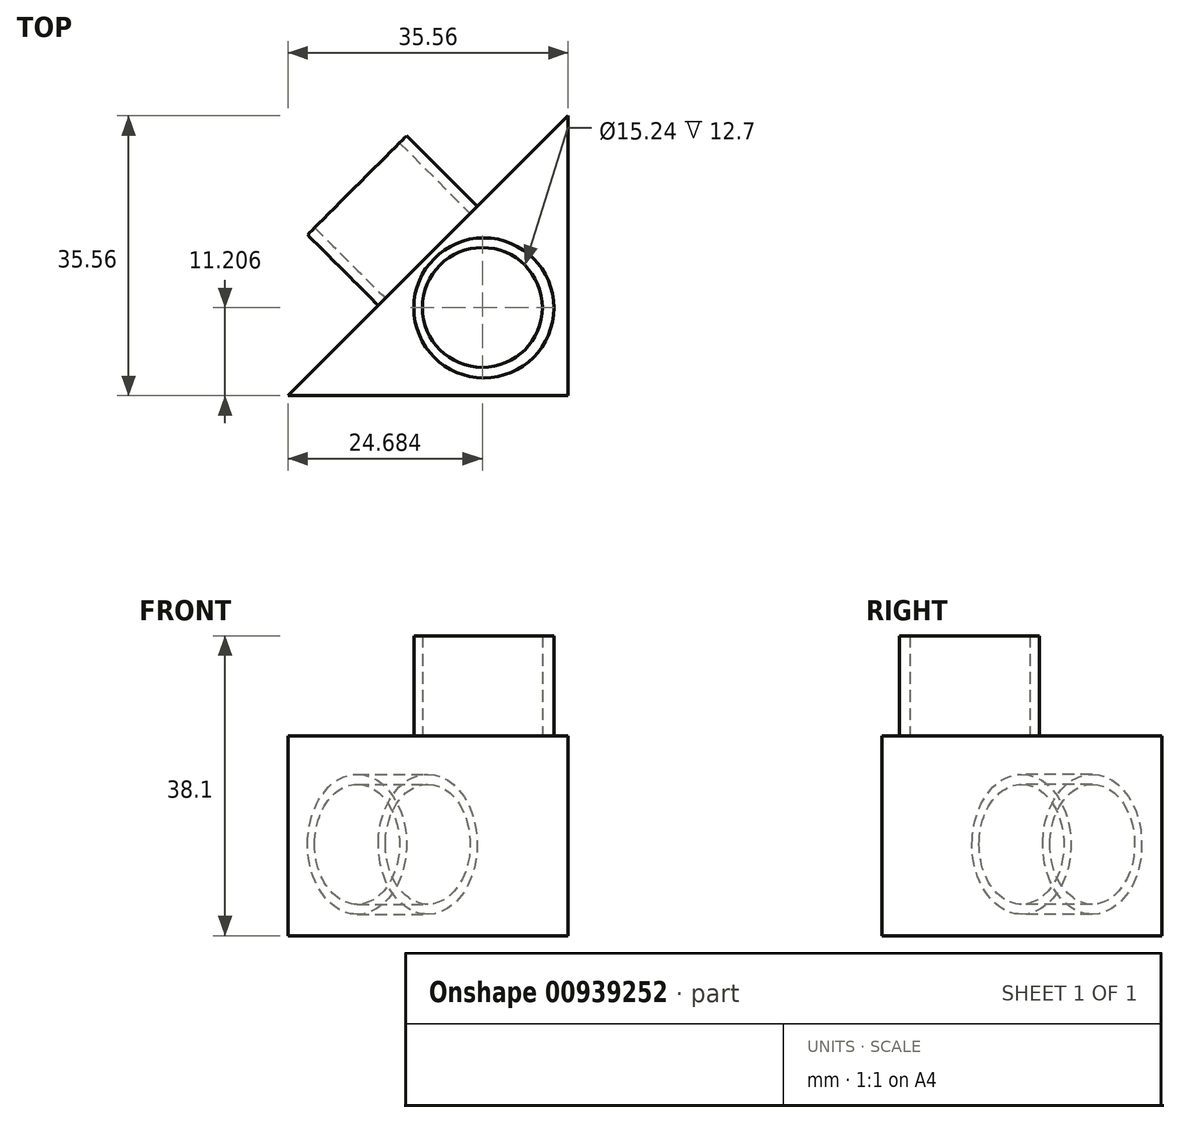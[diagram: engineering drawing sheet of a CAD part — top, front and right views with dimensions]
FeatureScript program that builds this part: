
annotation { "Feature Type Name" : "Feature", "Feature Type Description" : "" }
export const myFeature = defineFeature(function(context is Context, id is Id, definition is map)
    precondition{}
    {
        {
            var Q0;
            Q0=qCreatedBy(makeId("Top.planeOp"),FACE);
            var sketch = newSketch(context, id + "F0", { "sketchPlane" : qUnion([Q0])});
            skLineSegment(sketch, "E0", {"start": v(-60.17, 0) * mm, "end": v(-24.61, 35.56) * mm});
            skLineSegment(sketch, "E1", {"start": v(-24.61, 35.56) * mm, "end": v(-24.61, 0) * mm});
            skLineSegment(sketch, "E2", {"start": v(-24.61, 0) * mm, "end": v(-60.17, 0) * mm});
            skSolve(sketch);
        }
        {
            var Q0;
            Q0=makeQuery(id+"F0.imprint","IMPRINT",FACE,{"disambiguationData":[TD([[makeQuery(id+"F0.imprint","IMPRINT",EDGE,{"derivedFrom":sQuery(id+"F0.wireOp",EDGE,"E0")}),-1.0]])]});
            extrude(context, id + "F1", {"entities" : qUnion([Q0]), "depth" : 25.4 * mm, "offsetDistance" : 25.4 * mm});
        }
        {
            var Q0;
            Q0=makeQuery(id+"F1.opExtrude","CAP_FACE",FACE,{"disambiguationData":[OSD([sQuery(id+"F0.wireOp",EDGE,"E0"),sQuery(id+"F0.wireOp",EDGE,"E1"),sQuery(id+"F0.wireOp",EDGE,"E2")])],"isStart":false});
            var sketch = newSketch(context, id + "F2", { "sketchPlane" : qUnion([Q0])});
            skCircle(sketch, "E3", {"center": v(-35.49, 11.2) * mm, "radius": 7.62 * mm});
            skSolve(sketch);
        }
        {
            var Q0;
            Q0=makeQuery(id+"F2.imprint","IMPRINT",FACE,{"disambiguationData":[TD([[makeQuery(id+"F2.imprint","IMPRINT",EDGE,{"derivedFrom":sQuery(id+"F2.wireOp",EDGE,"E3")}),-1.0]])]});
            var sketch = newSketch(context, id + "F3", { "sketchPlane" : qUnion([Q0])});
            skCircle(sketch, "E4", {"center": v(-35.3, 11.16) * mm, "radius": 8.9 * mm});
            skSolve(sketch);
        }
        {
            var Q0;
            Q0 = qSketchRegion(id + "F3", true);
            extrude(context, id + "F4", {"entities" : qUnion([Q0]), "operationType" : NewBodyOperationType.ADD, "depth" : 12.7 * mm, "offsetDistance" : 25.4 * mm});
        }
        {
            var Q0;
            Q0 = qSketchRegion(id + "F2", true);
            extrude(context, id + "F5", {"entities" : qUnion([Q0]), "operationType" : NewBodyOperationType.REMOVE, "depth" : 39.12 * mm, "offsetDistance" : 25.4 * mm});
        }
        {
            var Q0;
            Q0=makeQuery(id+"F1.opExtrude","SWEPT_FACE",FACE,{"disambiguationData":[OSD([sQuery(id+"F0.wireOp",EDGE,"E0")])]});
            var sketch = newSketch(context, id + "F6", { "sketchPlane" : qUnion([Q0])});
            skCircle(sketch, "E5", {"center": v(17.44, 11.61) * mm, "radius": 7.62 * mm});
            skCircle(sketch, "E6", {"center": v(17.44, 11.61) * mm, "radius": 8.9 * mm});
            skSolve(sketch);
        }
        {
            var Q0;
            Q0=makeQuery(id+"F6.imprint","IMPRINT",FACE,{"disambiguationData":[TD([[makeQuery(id+"F6.imprint","IMPRINT",EDGE,{"derivedFrom":sQuery(id+"F6.wireOp",EDGE,"E5")}),-1.0]])]});
            extrude(context, id + "F7", {"entities" : qUnion([Q0]), "operationType" : NewBodyOperationType.ADD, "depth" : 12.7 * mm, "offsetDistance" : 25.4 * mm});
        }
    });
